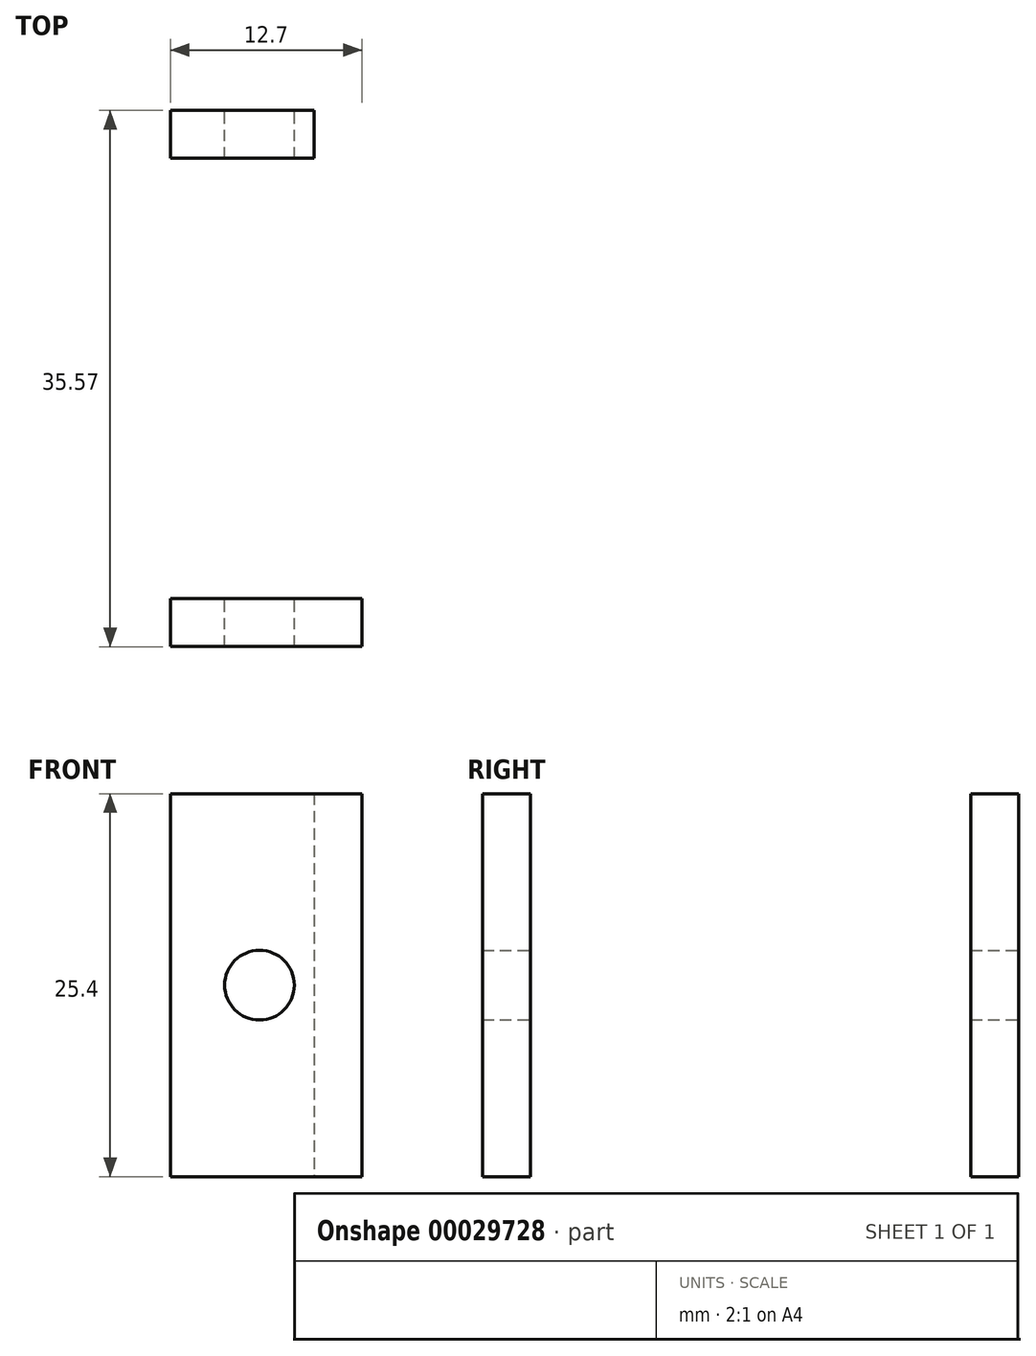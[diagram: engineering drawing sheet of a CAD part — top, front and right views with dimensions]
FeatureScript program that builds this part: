
annotation { "Feature Type Name" : "Feature", "Feature Type Description" : "" }
export const myFeature = defineFeature(function(context is Context, id is Id, definition is map)
    precondition{}
    {
        {
            var Q0;
            Q0=qCreatedBy(makeId("Top.planeOp"),FACE);
            var sketch = newSketch(context, id + "F0", { "sketchPlane" : qUnion([Q0])});
            skLineSegment(sketch, "E0.bottom", {"start": v(-5.9, -29.21) * mm, "end": v(6.8, -29.21) * mm});
            skLineSegment(sketch, "E0.top", {"start": v(-5.9, -32.38) * mm, "end": v(6.8, -32.38) * mm});
            skLineSegment(sketch, "E0.left", {"start": v(-5.9, -29.21) * mm, "end": v(-5.9, -32.38) * mm});
            skLineSegment(sketch, "E0.right", {"start": v(6.8, -29.2) * mm, "end": v(6.8, -32.38) * mm});
            skLineSegment(sketch, "E1.bottom", {"start": v(6.8, -29.2) * mm, "end": v(3.62, -29.2) * mm});
            skLineSegment(sketch, "E1.top", {"start": v(6.8, 3.18) * mm, "end": v(3.62, 3.18) * mm});
            skLineSegment(sketch, "E1.left", {"start": v(6.8, -29.2) * mm, "end": v(6.8, 3.18) * mm});
            skLineSegment(sketch, "E1.right", {"start": v(3.62, -29.2) * mm, "end": v(3.62, 3.18) * mm});
            skLineSegment(sketch, "E2.bottom", {"start": v(3.62, 3.18) * mm, "end": v(-5.9, 3.18) * mm});
            skLineSegment(sketch, "E2.top", {"start": v(3.62, 0) * mm, "end": v(-5.9, 0) * mm});
            skLineSegment(sketch, "E2.left", {"start": v(3.62, 3.18) * mm, "end": v(3.62, 0) * mm});
            skLineSegment(sketch, "E2.right", {"start": v(-5.9, 3.18) * mm, "end": v(-5.9, 0) * mm});
            skSolve(sketch);
        }
        {
            var Q0;
            Q0=makeQuery(id+"F0.imprint","IMPRINT",FACE,{"disambiguationData":[TD([[makeQuery(id+"F0.imprint","IMPRINT",EDGE,{"derivedFrom":sQuery(id+"F0.wireOp",EDGE,"E1.bottom")}),-1.0]])]});
            var Q1;
            Q1=makeQuery(id+"F0.imprint","IMPRINT",FACE,{"disambiguationData":[TD([[makeQuery(id+"F0.imprint","IMPRINT",EDGE,{"derivedFrom":sQuery(id+"F0.wireOp",EDGE,"E0.bottom")}),-1.0]])]});
            var Q2;
            Q2=makeQuery(id+"F0.imprint","IMPRINT",FACE,{"disambiguationData":[TD([[makeQuery(id+"F0.imprint","IMPRINT",EDGE,{"derivedFrom":sQuery(id+"F0.wireOp",EDGE,"E2.bottom")}),1.0]])]});
            extrude(context, id + "F1", {"entities" : qUnion([Q0, Q1, Q2]), "depth" : 25.4 * mm});
        }
        {
            var Q0;
            Q0=makeQuery(id+"F1.opExtrude","SWEPT_FACE",FACE,{"disambiguationData":[OSD([sQuery(id+"F0.wireOp",EDGE,"E1.top"),sQuery(id+"F0.wireOp",EDGE,"E2.bottom")])]});
            var sketch = newSketch(context, id + "F2", { "sketchPlane" : qUnion([Q0])});
            skCircle(sketch, "E3", {"center": v(0, 12.7) * mm, "radius": 2.31 * mm});
            skSolve(sketch);
        }
        {
            var Q0;
            Q0=makeQuery(id+"F2.imprint","IMPRINT",FACE,{"disambiguationData":[TD([[makeQuery(id+"F2.imprint","IMPRINT",EDGE,{"derivedFrom":sQuery(id+"F2.wireOp",EDGE,"E3")}),1.0]])]});
            extrude(context, id + "F3", {"entities" : qUnion([Q0]), "operationType" : NewBodyOperationType.REMOVE, "oppositeDirection" : true, "depth" : 84.27 * mm});
        }
    });
